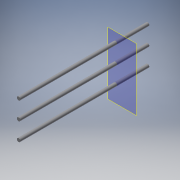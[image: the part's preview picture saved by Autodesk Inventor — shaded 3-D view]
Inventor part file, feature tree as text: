
AUTODESK INVENTOR PART (.ipt)
format: ipt  version: 2016 (Build 200138000, 138)  size: 109,056 bytes
history: native  units: in
note: dims shown in document units (in); Inventor stores cm internally (conversion verified against a paired STEP export)
features: plane x1, extrude x1, sketch x1, reference x1
ambient origin geometry x8: Origin, YZ Plane, XZ Plane, XY Plane, X Axis, Y Axis, Z Axis, Center Point
bodies: Solid1 (feature_tree)
feature tree (4):
  plane  "Work Plane1"
  extrude  "Extrusion1"  Depth=0.7874in
  sketch  "Sketch1"  dims[d0=0.315in d1=0.315in d2=0.315in d3=2.9528in d4=8.8583in d5=0.0in d6=0.0in d7=0.7874in d8=0.7874in]
  reference  "Reference1"
